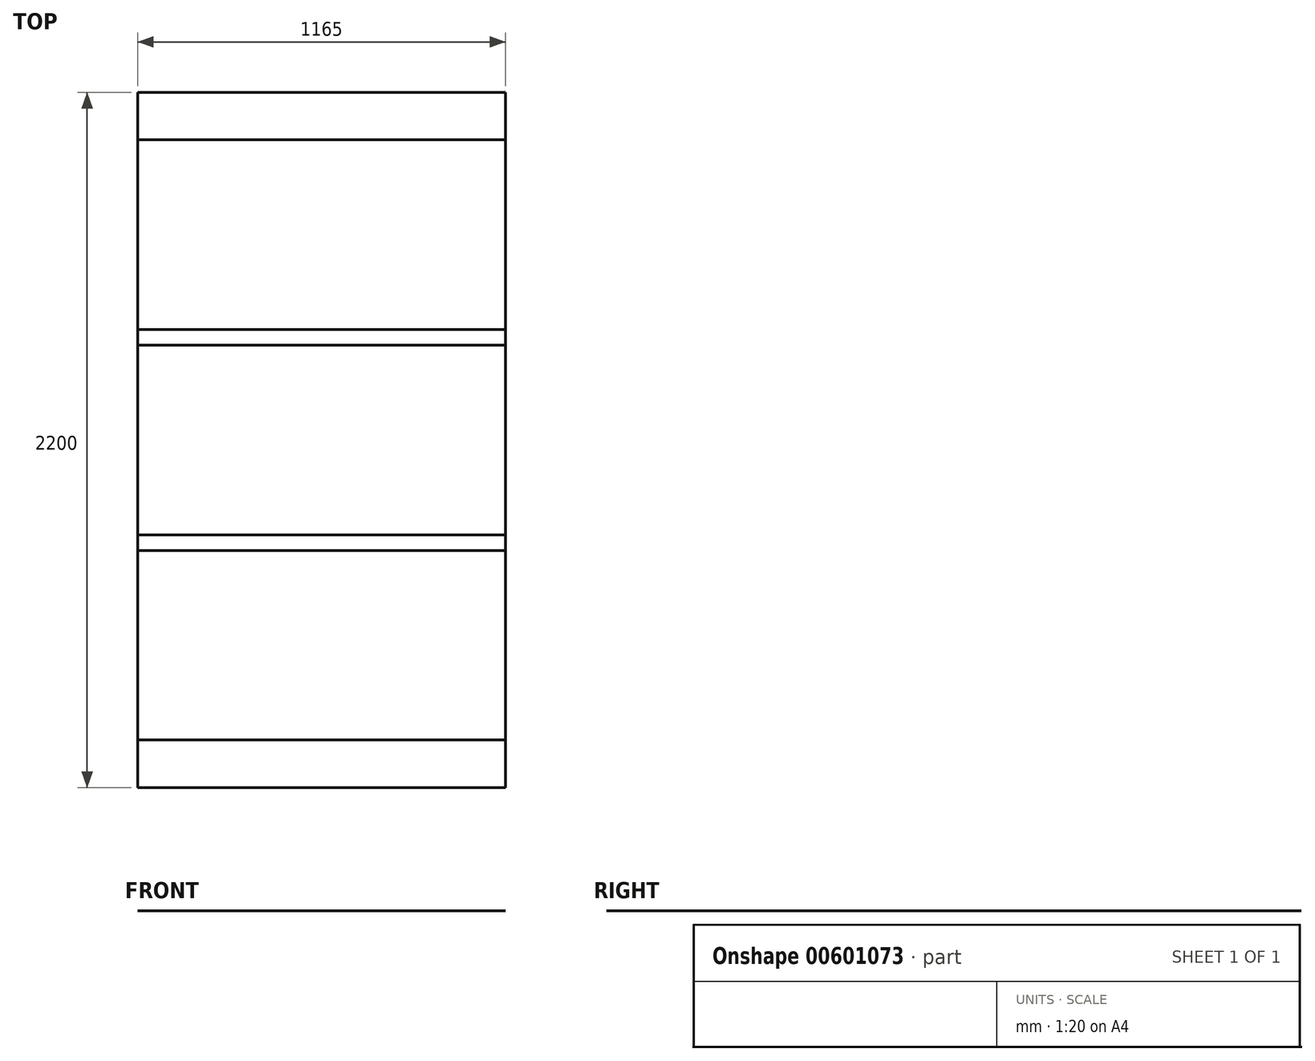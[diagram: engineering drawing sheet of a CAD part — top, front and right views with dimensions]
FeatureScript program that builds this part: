
annotation { "Feature Type Name" : "Feature", "Feature Type Description" : "" }
export const myFeature = defineFeature(function(context is Context, id is Id, definition is map)
    precondition{}
    {
        {
            var Q0;
            Q0=qCreatedBy(makeId("Right.planeOp"),FACE);
            var sketch = newSketch(context, id + "F0", { "sketchPlane" : qUnion([Q0])});
            skLineSegment(sketch, "E0", {"start": v(0, 0) * mm, "end": v(-150, 0) * mm});
            skSolve(sketch);
        }
        {
            var Q0;
            Q0=sQuery(id+"F0.wireOp",EDGE,"E0");
            extrude(context, id + "F1", {"bodyType" : ToolBodyType.SURFACE, "surfaceEntities" : qUnion([Q0]), "depth" : 1165 * mm, "offsetDistance" : 25 * mm});
        }
        {
            var Q0;
            Q0=qCreatedBy(makeId("Right.planeOp"),FACE);
            var sketch = newSketch(context, id + "F2", { "sketchPlane" : qUnion([Q0])});
            skLineSegment(sketch, "E1", {"start": v(-150, 0) * mm, "end": v(-750, 0) * mm});
            skSolve(sketch);
        }
        {
            var Q0;
            Q0 = qSketchRegion(id + "F2", true);
            var Q1;
            Q1=sQuery(id+"F2.wireOp",EDGE,"E1");
            extrude(context, id + "F3", {"entities" : qUnion([Q0]), "bodyType" : ToolBodyType.SURFACE, "surfaceEntities" : qUnion([Q1]), "depth" : 1165 * mm, "offsetDistance" : 25 * mm});
        }
        {
            var Q0;
            Q0=qCreatedBy(makeId("Right.planeOp"),FACE);
            var sketch = newSketch(context, id + "F4", { "sketchPlane" : qUnion([Q0])});
            skLineSegment(sketch, "E2", {"start": v(-750, 0) * mm, "end": v(-800, 0) * mm});
            skSolve(sketch);
        }
        {
            var Q0;
            Q0=sQuery(id+"F4.wireOp",EDGE,"E2");
            extrude(context, id + "F5", {"bodyType" : ToolBodyType.SURFACE, "surfaceEntities" : qUnion([Q0]), "depth" : 1165 * mm, "offsetDistance" : 25 * mm});
        }
        {
            var Q0;
            Q0=qCreatedBy(makeId("Right.planeOp"),FACE);
            var sketch = newSketch(context, id + "F6", { "sketchPlane" : qUnion([Q0])});
            skLineSegment(sketch, "E3", {"start": v(-800, 0) * mm, "end": v(-1400, 0) * mm});
            skSolve(sketch);
        }
        {
            var Q0;
            Q0=sQuery(id+"F6.wireOp",EDGE,"E3");
            extrude(context, id + "F7", {"bodyType" : ToolBodyType.SURFACE, "surfaceEntities" : qUnion([Q0]), "depth" : 1165 * mm, "offsetDistance" : 25 * mm});
        }
        {
            var Q0;
            Q0=qCreatedBy(makeId("Right.planeOp"),FACE);
            var sketch = newSketch(context, id + "F8", { "sketchPlane" : qUnion([Q0])});
            skLineSegment(sketch, "E4", {"start": v(-1400, 0) * mm, "end": v(-1450, 0) * mm});
            skSolve(sketch);
        }
        {
            var Q0;
            Q0=sQuery(id+"F8.wireOp",EDGE,"E4");
            extrude(context, id + "F9", {"bodyType" : ToolBodyType.SURFACE, "surfaceEntities" : qUnion([Q0]), "depth" : 1165 * mm, "offsetDistance" : 25 * mm});
        }
        {
            var Q0;
            Q0=qCreatedBy(makeId("Right.planeOp"),FACE);
            var sketch = newSketch(context, id + "F10", { "sketchPlane" : qUnion([Q0])});
            skLineSegment(sketch, "E5", {"start": v(-1450, 0) * mm, "end": v(-2050, 0) * mm});
            skSolve(sketch);
        }
        {
            var Q0;
            Q0=sQuery(id+"F10.wireOp",EDGE,"E5");
            extrude(context, id + "F11", {"bodyType" : ToolBodyType.SURFACE, "surfaceEntities" : qUnion([Q0]), "depth" : 1165 * mm, "offsetDistance" : 25 * mm});
        }
        {
            var Q0;
            Q0=qCreatedBy(makeId("Right.planeOp"),FACE);
            var sketch = newSketch(context, id + "F12", { "sketchPlane" : qUnion([Q0])});
            skLineSegment(sketch, "E6", {"start": v(-2050, 0) * mm, "end": v(-2200, 0) * mm});
            skSolve(sketch);
        }
        {
            var Q0;
            Q0=sQuery(id+"F12.wireOp",EDGE,"E6");
            extrude(context, id + "F13", {"bodyType" : ToolBodyType.SURFACE, "surfaceEntities" : qUnion([Q0]), "depth" : 1165 * mm, "offsetDistance" : 25 * mm});
        }
    });
